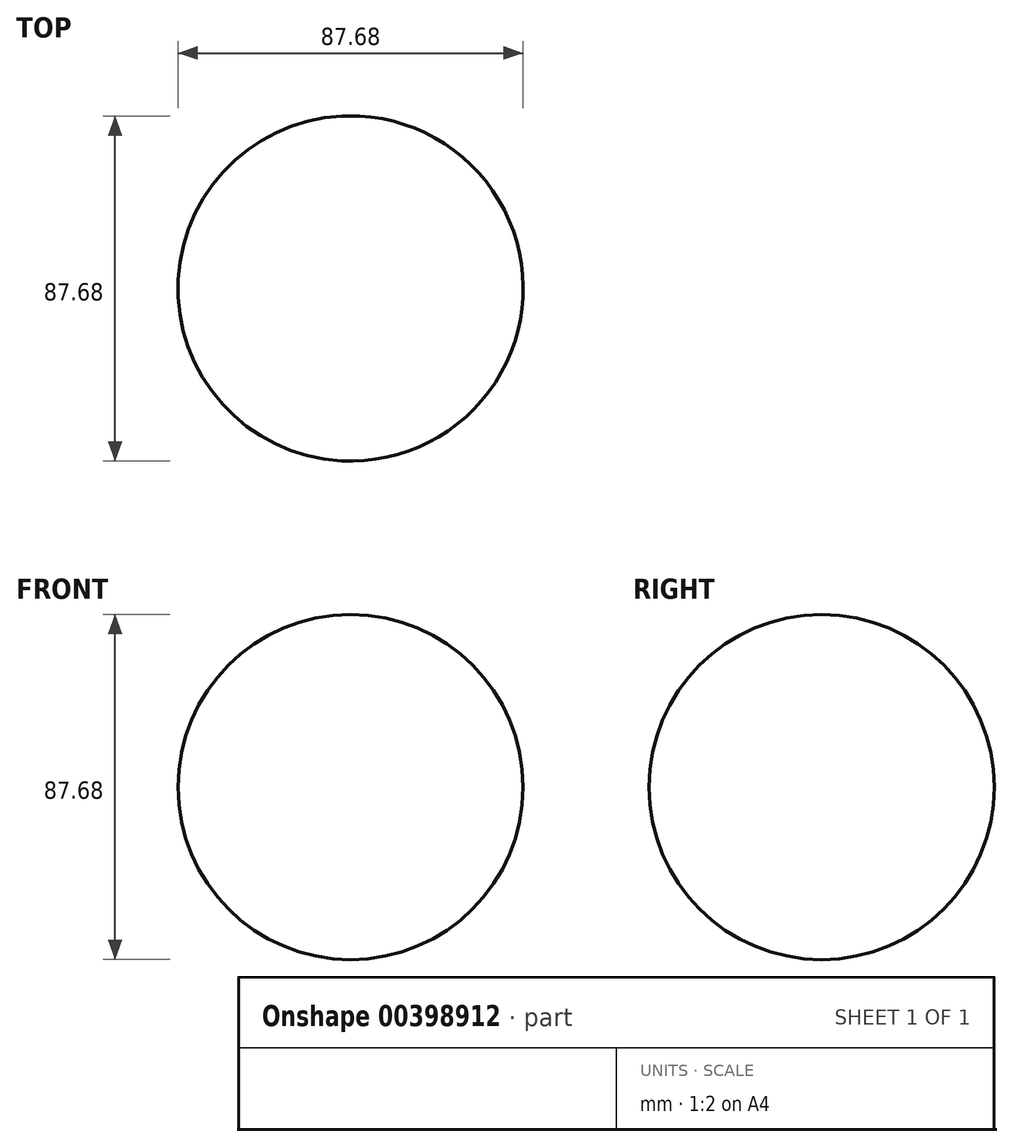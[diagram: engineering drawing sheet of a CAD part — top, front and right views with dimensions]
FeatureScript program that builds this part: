
annotation { "Feature Type Name" : "Feature", "Feature Type Description" : "" }
export const myFeature = defineFeature(function(context is Context, id is Id, definition is map)
    precondition{}
    {
        {
            var Q0;
            Q0=qCreatedBy(makeId("Top.planeOp"),FACE);
            var sketch = newSketch(context, id + "F0", { "sketchPlane" : qUnion([Q0])});
            skLineSegment(sketch, "E0", {"start": v(-195.51, -116.25) * mm, "end": v(-217.18, -173.4) * mm});
            skLineSegment(sketch, "E1", {"start": v(-195.51, -116.25) * mm, "end": v(-183.8, -173.4) * mm});
            skLineSegment(sketch, "E2", {"start": v(-142.56, -159.19) * mm, "end": v(-151.25, -325.47) * mm});
            skCircle(sketch, "E3", {"center": v(-145.94, -223.96) * mm, "radius": 43.84 * mm});
            skSolve(sketch);
        }
        {
            var Q0;
            {var subQ0=sQuery(id+"F0.wireOp",EDGE,"E3");var subQ1=sQuery(id+"F0.wireOp",EDGE,"E2");var subQ2=makeQuery(id+"F0.imprint","INTERSECT",VERTEX,{"disambiguationData":[OD(0.0)],"derivedFrom":[subQ1,subQ0]});Q0=makeQuery(id+"F0.imprint","IMPRINT",FACE,{"disambiguationData":[TD([[makeQuery(id+"F0.imprint","IMPRINT",EDGE,{"disambiguationData":[TD([[subQ2,1.0]])],"derivedFrom":subQ1}),1.0]])]});}
            var Q1;
            Q1=sQuery(id+"F0.wireOp",EDGE,"E2");
            revolve(context, id + "F1", {"entities" : qUnion([Q0]), "axis" : qUnion([Q1]), "revolveType" : RevolveType.FULL});
        }
    });
